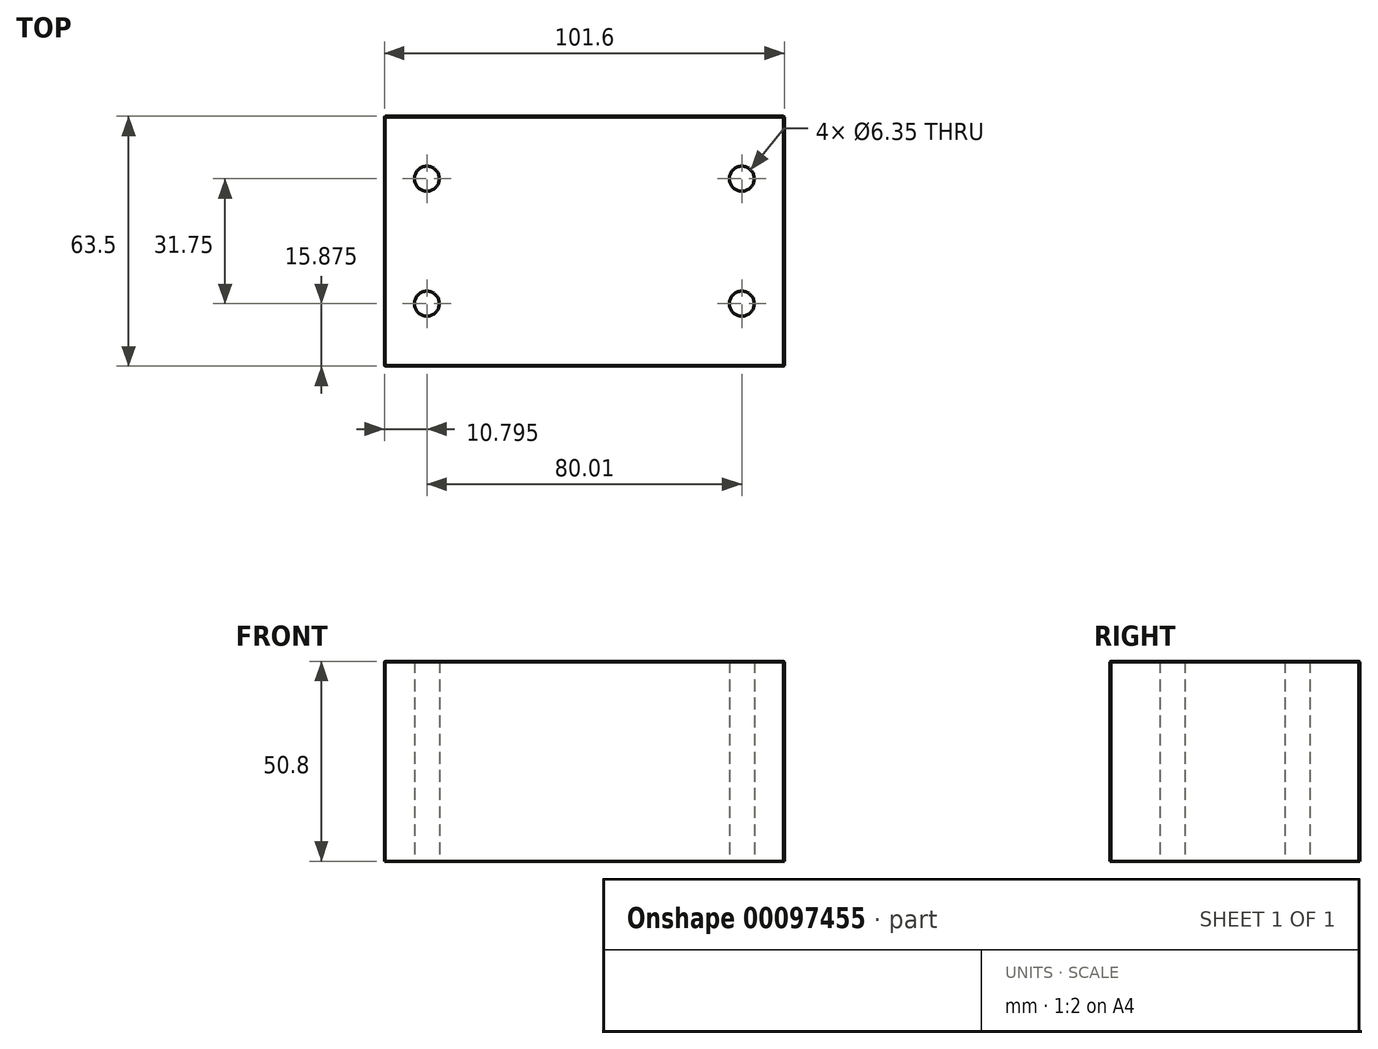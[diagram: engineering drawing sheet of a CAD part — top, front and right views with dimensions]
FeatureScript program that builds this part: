
annotation { "Feature Type Name" : "Feature", "Feature Type Description" : "" }
export const myFeature = defineFeature(function(context is Context, id is Id, definition is map)
    precondition{}
    {
        {
            var Q0;
            Q0=qCreatedBy(makeId("Top.planeOp"),FACE);
            var sketch = newSketch(context, id + "F0", { "sketchPlane" : qUnion([Q0])});
            skLineSegment(sketch, "E0.bottom", {"start": v(0, 0) * mm, "end": v(101.6, 0) * mm});
            skLineSegment(sketch, "E0.top", {"start": v(0, 63.5) * mm, "end": v(101.6, 63.5) * mm});
            skLineSegment(sketch, "E0.left", {"start": v(0, 0) * mm, "end": v(0, 63.5) * mm});
            skLineSegment(sketch, "E0.right", {"start": v(101.6, 0) * mm, "end": v(101.6, 63.5) * mm});
            skCircle(sketch, "E1", {"center": v(10.8, 47.63) * mm, "radius": 3.18 * mm});
            skLineSegment(sketch, "E2", {"start": v(10.8, 47.63) * mm, "end": v(10.8, 15.88) * mm, "construction": true});
            skCircle(sketch, "E3", {"center": v(10.8, 15.88) * mm, "radius": 3.18 * mm});
            skLineSegment(sketch, "E4", {"start": v(50.8, 63.5) * mm, "end": v(50.8, 0) * mm, "construction": true});
            skCircle(sketch, "E5.MirrorC", {"center": v(90.8, 15.88) * mm, "radius": 3.18 * mm});
            skCircle(sketch, "E6.MirrorC", {"center": v(90.8, 47.63) * mm, "radius": 3.18 * mm});
            skSolve(sketch);
        }
        {
            var Q0;
            Q0=makeQuery(id+"F0.imprint","IMPRINT",FACE,{"disambiguationData":[TD([[makeQuery(id+"F0.imprint","IMPRINT",EDGE,{"derivedFrom":sQuery(id+"F0.wireOp",EDGE,"E0.bottom")}),1.0]])]});
            extrude(context, id + "F1", {"entities" : qUnion([Q0]), "depth" : 50.8 * mm});
        }
        {
            var Q0;
            Q0=makeQuery(id+"F1.opExtrude","CAP_EDGE",EDGE,{"disambiguationData":[OSD([sQuery(id+"F0.wireOp",EDGE,"E0.left")])],"isStart":false});
            var Q1;
            Q1=makeQuery(id+"F1.opExtrude","CAP_EDGE",EDGE,{"disambiguationData":[OSD([sQuery(id+"F0.wireOp",EDGE,"E0.bottom")])],"isStart":false});
            var Q2;
            Q2=makeQuery(id+"F1.opExtrude","CAP_EDGE",EDGE,{"disambiguationData":[OSD([sQuery(id+"F0.wireOp",EDGE,"E0.top")])],"isStart":false});
            var Q3;
            Q3=makeQuery(id+"F1.opExtrude","CAP_EDGE",EDGE,{"disambiguationData":[OSD([sQuery(id+"F0.wireOp",EDGE,"E0.right")])],"isStart":false});
            var Q4;
            Q4=makeQuery(id+"F1.opExtrude","SWEPT_EDGE",EDGE,{"disambiguationData":[OSD([sQuery(id+"F0.wireOp",EDGE,"E0.bottom"),sQuery(id+"F0.wireOp",EDGE,"E0.right")])]});
            var Q5;
            Q5=makeQuery(id+"F1.opExtrude","SWEPT_EDGE",EDGE,{"disambiguationData":[OSD([sQuery(id+"F0.wireOp",EDGE,"E0.top"),sQuery(id+"F0.wireOp",EDGE,"E0.right")])]});
            var Q6;
            Q6=makeQuery(id+"F1.opExtrude","SWEPT_EDGE",EDGE,{"disambiguationData":[OSD([sQuery(id+"F0.wireOp",EDGE,"E0.bottom"),sQuery(id+"F0.wireOp",EDGE,"E0.left")])]});
            var Q7;
            Q7=makeQuery(id+"F1.opExtrude","SWEPT_EDGE",EDGE,{"disambiguationData":[OSD([sQuery(id+"F0.wireOp",EDGE,"E0.top"),sQuery(id+"F0.wireOp",EDGE,"E0.left")])]});
            chamfer(context, id + "F2", {"entities" : qUnion([Q0, Q1, Q2, Q3, Q4, Q5, Q6, Q7]), "width" : 0.2 * mm, "tangentPropagation" : true});
        }
    });
